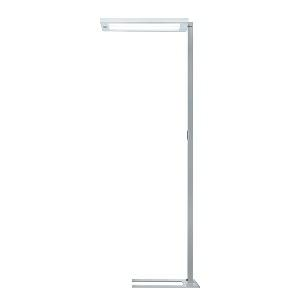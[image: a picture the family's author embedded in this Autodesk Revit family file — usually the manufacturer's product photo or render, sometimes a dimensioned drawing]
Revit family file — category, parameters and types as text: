
# Revit family: lavigo_-_dps_14000_vtl_r_g2_00800396_bd87
name_source: partatom
category: Lighting Fixtures
units: mm (PartAtom-declared; Revit-internal decimal feet)

## family parameters
Cut with Voids When Loaded = No
Host = Face
Light Source = No
Part Type = Normal
Room Calculation Point = No
Round Connector Dimension = Use Diameter
Shared = No

## types (1)
- LAVIGO - DPS 14000/VTL/R/G2 (1 x LED VTL, 14250 lm, 3000-6500K)
    Apparent Load = 100 VA
    Approval mark = CE
    CIE Flux Codes = 60 87 97 12 100
    Color Rendering = 80-89
    Color Temperature = 3000-6500K
    Control Gear = Electronic ballast
    Default Elevation = 1800 mm
    Description = DPS 14000/VTL/R/G2|Free-standing luminaire|light source: LED  3000-6500 K  Energy efficiency category A/A+/A++|LED  4000 K 4000 K Energy efficiency category A/A+/A++|work equipment: Electronic ballast|connected load: 220-240 V, 50/60 Hz|Power consumption: approx. 100 W|standby: approx. 0,50|power factor: approx. 0,965|luminous flux: 14250 lm|luminous efficacy: 142 lm/W|light distribution: Direct/indirect|direct ratio: approx. 12 %|color rendering index (CRI): >= 80|technology: Presence and daylight sensor control (PIR)|operation: Multi-function switch|luminaire body|material: Steel/plastic|surface: Painted|colour: Silver metallic|lamp cover: Acrylic (PMMA), Satine|tubular section|material: Steel tube|surface: Painted|Form: Tubular section upright|colour of tubular section: Silver metallic|luminaire base|Form: C-form flat|weight (net): approx. 19.7 kg|mains lead: 3.00 m Mains plug CEE 7/VII|Fastening: Floor standing base|decorative contrast side parts: Flint grey|glare control: Prism aperture|luminance(L65): <= 3000 cd/m|unified glare rating(4H 8H): <=  16|special features: Luminaire head detachable, Cradle to Cradle Certified TM, Direct light component with edge light and light-guide technology for homogenous light exit, Flicker-free, Indirect light component biodynamic light VTL, direct light component neutral working light, Integrated light and presence sensor PIR, Integrated light management for biodynamic light VTL, Retrofittable with TALK module, Separated, direct and indirect light individually adjustable|
    Frequency = 50 Hz
    Height = 36 mm
    Lamp = 1 x LED VTL
    Lamp Light Flux = 14250 lm
    Lamp count = 1
    Length = 675 mm
    Luminous efficacy = 143 lm/W
    Manufacturer = Waldmann
    ModVariant = No
    Model = 00800396
    Mounting Place = Floor
    Mounting Type = Freestanding
    Number of Poles = 1
    OnlyDefault = Yes
    Power Factor = 1
    Product Name = LAVIGO - DPS 14000/VTL/R/G2
    Product group = Free standing luminaire
    ProductGroupID = 13
    Protection Class = Protection class I
    Protection Degree = IP 20
    RLX_Detail_Level = 1
    RLX_Emergency_Light_Flux = 0 lm
    RLX_Emergency_Type = 0
    RLX_Emergency_Type_DB = No
    RlxData = <blob elided: 37385 chars, md5=d171fceb>
    Socket = socket
    Standby Power = 0 W
    System Light Flux = 14250 lm
    System Power = 100 W
    Type Comments = Product without accessories
    Type Image = 121695000-00625713.jpg
    URL = http://relux.com
    VarID = ---
    Voltage = 230 V
    Voltage Range = 220-240 V
    Weight = 0.00 kg
    Width = 320 mm

## geometry (parser evidence)
native form markers: Blend x4, Sweep x14
no freeform markers — native parametric forms only
